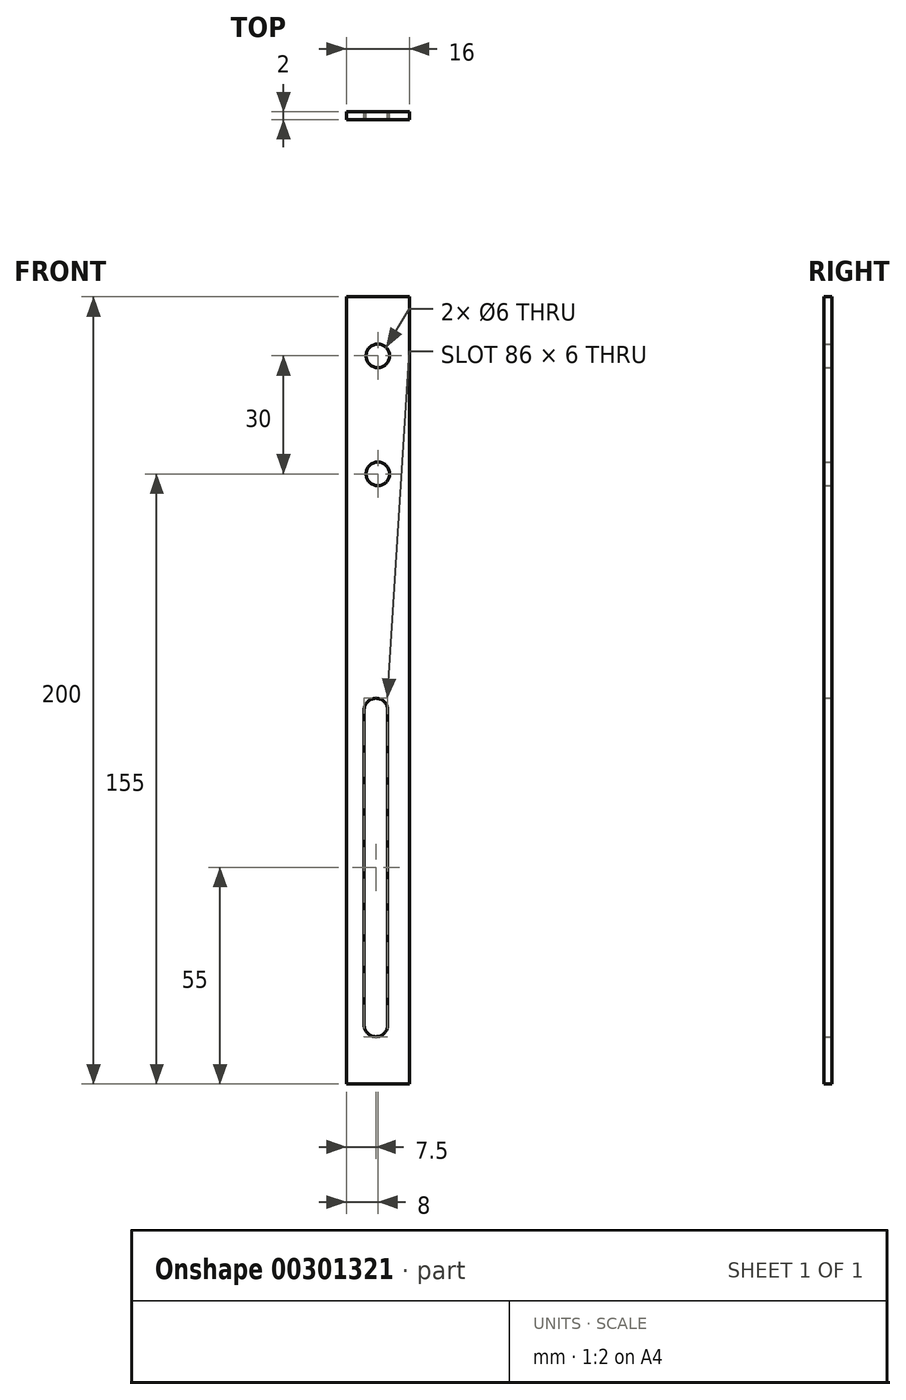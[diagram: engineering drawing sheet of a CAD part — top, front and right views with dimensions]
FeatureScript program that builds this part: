
annotation { "Feature Type Name" : "Feature", "Feature Type Description" : "" }
export const myFeature = defineFeature(function(context is Context, id is Id, definition is map)
    precondition{}
    {
        {
            var Q0;
            Q0=qCreatedBy(makeId("Front.planeOp"),FACE);
            var sketch = newSketch(context, id + "F0", { "sketchPlane" : qUnion([Q0])});
            skLineSegment(sketch, "E0.bottom", {"start": v(0, 0) * mm, "end": v(16, 0) * mm});
            skLineSegment(sketch, "E0.top", {"start": v(0, 200) * mm, "end": v(16, 200) * mm});
            skLineSegment(sketch, "E0.left", {"start": v(0, 0) * mm, "end": v(0, 200) * mm});
            skLineSegment(sketch, "E0.right", {"start": v(16, 0) * mm, "end": v(16, 200) * mm});
            skCircle(sketch, "E1", {"center": v(8, 185) * mm, "radius": 3 * mm});
            skPoint(sketch, "E2", {"position": v(8, 200) * mm});
            skCircle(sketch, "E3.0.1.0", {"center": v(8, 155) * mm, "radius": 3 * mm});
            skLineSegment(sketch, "E3.direction1", {"start": v(8, 185) * mm, "end": v(32.5, 185) * mm, "construction": true});
            skLineSegment(sketch, "E3.direction2", {"start": v(8, 185) * mm, "end": v(8, 155) * mm, "construction": true});
            skLineSegment(sketch, "E4", {"start": v(4.5, 95) * mm, "end": v(4.5, 15) * mm});
            skLineSegment(sketch, "E5", {"start": v(10.5, 95) * mm, "end": v(10.5, 15) * mm});
            skArc(sketch, "E6", {"start": v(4.5, 15) * mm, "mid": v(7.5, 12) * mm, "end": v(10.5, 15) * mm});
            skArc(sketch, "E7", {"start": v(10.5, 95) * mm, "mid": v(7.5, 98) * mm, "end": v(4.5, 95) * mm});
            skSolve(sketch);
        }
        {
            var Q0;
            Q0=qSketchRegion(id+"F0",true);
            extrude(context, id + "F1", {"entities" : qUnion([Q0]), "depth" : 2 * mm});
        }
    });
